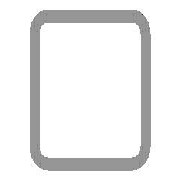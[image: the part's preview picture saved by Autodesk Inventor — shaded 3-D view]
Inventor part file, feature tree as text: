
AUTODESK INVENTOR PART (.ipt)
format: ipt  version: 2025 (Build 290162010, 162A)  size: 134,656 bytes
history: native  units: mm (DEFAULTED — no unit token found)
features: other x4, sketch x1, plane x1
ambient origin geometry x8: Origin, YZ Plane, XZ Plane, XY Plane, X Axis, Y Axis, Z Axis, Center Point
bodies: Solid1 (feature_tree), Body (feature_tree)
feature tree (6):
  parser-record x1  (decoder bookkeeping rows leaked as tree rows — omitted from the tree; the rows remain in map.json)
  other  "Driven Length"
  other  "Start Plane"
  other  "End Plane"
  sketch  "Sketch3"  dims[d3=1233.501073mm d4=0.0mm d7=6.0mm d9=80.0mm d11=80.0mm d12=3.0mm d13=80.0mm d14=1313.501073mm d15=40.0mm d16=40.0mm d17=90.0deg d18=1233.501073mm]
  plane  "Work Plane3"
